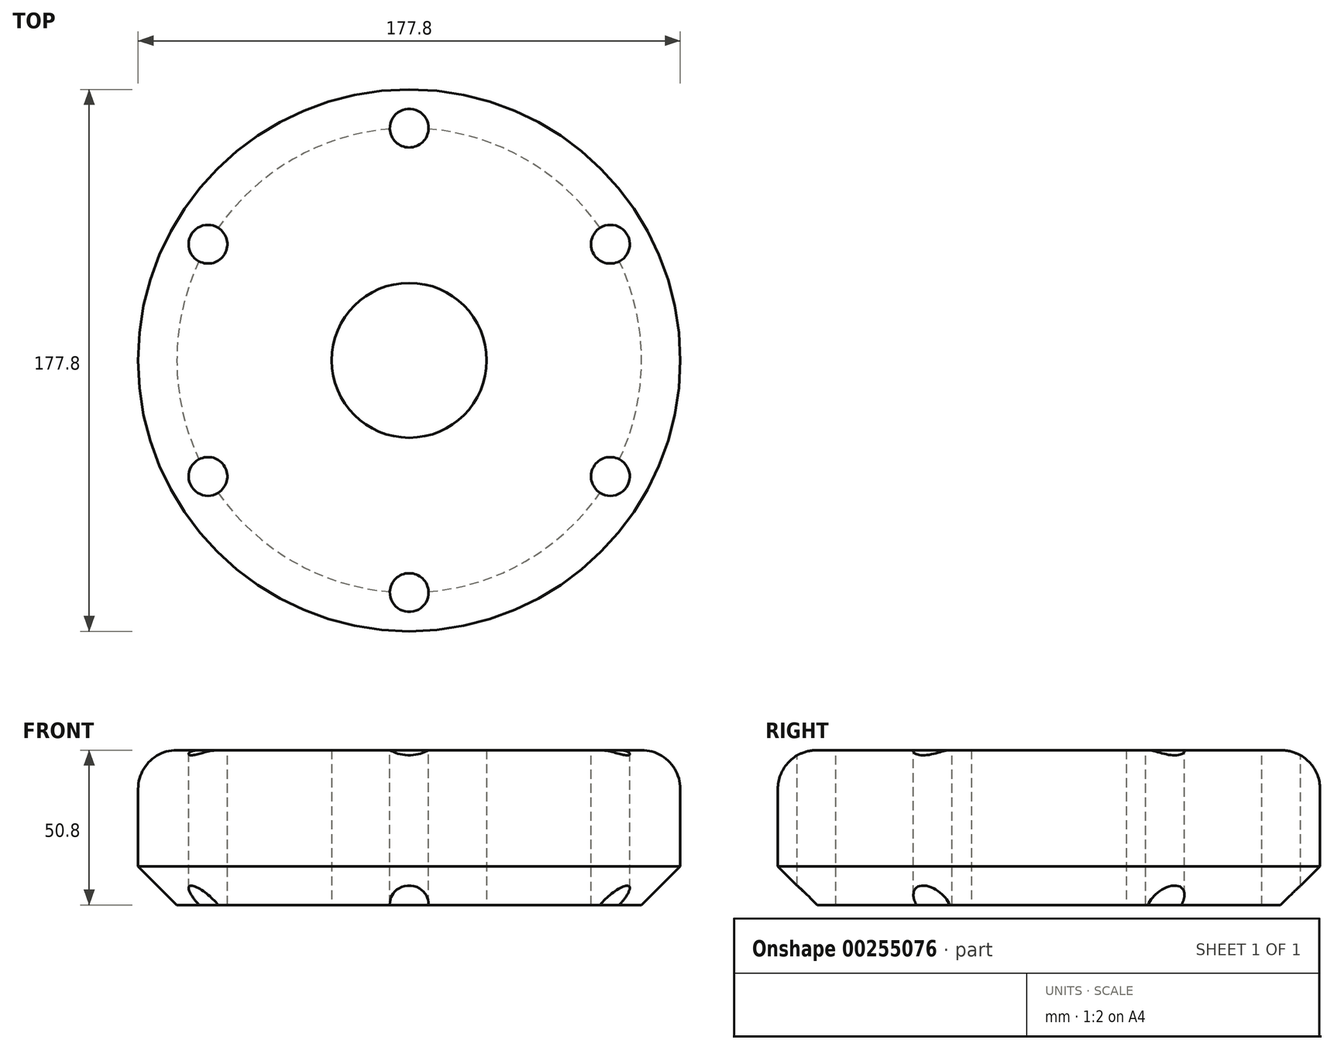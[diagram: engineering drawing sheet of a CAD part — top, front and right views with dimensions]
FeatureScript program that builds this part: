
annotation { "Feature Type Name" : "Feature", "Feature Type Description" : "" }
export const myFeature = defineFeature(function(context is Context, id is Id, definition is map)
    precondition{}
    {
        {
            var Q0;
            Q0=qCreatedBy(makeId("Front.planeOp"),FACE);
            var sketch = newSketch(context, id + "F0", { "sketchPlane" : qUnion([Q0])});
            skLineSegment(sketch, "E0", {"start": v(0, 0) * mm, "end": v(0, 127) * mm});
            skLineSegment(sketch, "E1.bottom", {"start": v(25.4, 0) * mm, "end": v(88.9, 0) * mm});
            skLineSegment(sketch, "E1.top", {"start": v(25.4, 50.8) * mm, "end": v(88.9, 50.8) * mm});
            skLineSegment(sketch, "E1.left", {"start": v(25.4, 0) * mm, "end": v(25.4, 50.8) * mm});
            skLineSegment(sketch, "E1.right", {"start": v(88.9, 0) * mm, "end": v(88.9, 50.8) * mm});
            skSolve(sketch);
        }
        {
            var Q0;
            Q0=makeQuery(id+"F0.imprint","IMPRINT",FACE,{"disambiguationData":[TD([[makeQuery(id+"F0.imprint","IMPRINT",EDGE,{"derivedFrom":sQuery(id+"F0.wireOp",EDGE,"E1.bottom")}),1.0]])]});
            var Q1;
            Q1=sQuery(id+"F0.wireOp",EDGE,"E0");
            revolve(context, id + "F1", {"entities" : qUnion([Q0]), "axis" : qUnion([Q1]), "revolveType" : RevolveType.FULL});
        }
        {
            var Q0;
            Q0=makeQuery(id+"F1.opRevolve","SWEPT_FACE",FACE,{"disambiguationData":[OSD([sQuery(id+"F0.wireOp",EDGE,"E1.top")])]});
            cPlane(context, id + "F2", {"entities" : qUnion([Q0]), "cplaneType" : CPlaneType.OFFSET, "offset" : 25.4 * mm, "width" : 152.4 * mm, "height" : 152.4 * mm});
        }
        {
            var Q0;
            Q0=qCreatedBy(id+"F2.planeOp",FACE);
            var sketch = newSketch(context, id + "F3", { "sketchPlane" : qUnion([Q0])});
            skCircle(sketch, "E2", {"center": v(0, 0) * mm, "radius": 76.2 * mm});
            skLineSegment(sketch, "E3", {"start": v(0, 0) * mm, "end": v(0, 76.2) * mm});
            skCircle(sketch, "E4", {"center": v(0, 76.2) * mm, "radius": 6.35 * mm});
            skCircle(sketch, "E5.1.0", {"center": v(66, 38.1) * mm, "radius": 6.35 * mm});
            skCircle(sketch, "E5.2.0", {"center": v(66, -38.1) * mm, "radius": 6.35 * mm});
            skCircle(sketch, "E5.3.0", {"center": v(0, -76.2) * mm, "radius": 6.35 * mm});
            skCircle(sketch, "E5.4.0", {"center": v(-66, -38.1) * mm, "radius": 6.35 * mm});
            skCircle(sketch, "E5.5.0", {"center": v(-66, 38.1) * mm, "radius": 6.35 * mm});
            skLineSegment(sketch, "E5.anchor1", {"start": v(0, 0) * mm, "end": v(0, 76.2) * mm, "construction": true});
            skLineSegment(sketch, "E5.anchor2", {"start": v(0, 0) * mm, "end": v(-66, 38.1) * mm, "construction": true});
            skSolve(sketch);
        }
        {
            var Q0;
            {var subQ0=sQuery(id+"F3.wireOp",EDGE,"E2");var subQ1=makeQuery(id+"F3.imprint","INTERSECT",VERTEX,{"derivedFrom":[subQ0,sQuery(id+"F3.wireOp",EDGE,"E3")]});Q0=makeQuery(id+"F3.imprint","IMPRINT",FACE,{"disambiguationData":[TD([[makeQuery(id+"F3.imprint","IMPRINT",EDGE,{"disambiguationData":[TD([[subQ1,1.0]])],"derivedFrom":subQ0}),-1.0]])]});}
            var Q1;
            {var subQ0=sQuery(id+"F3.wireOp",EDGE,"E3");var subQ1=sQuery(id+"F3.wireOp",EDGE,"E2");var subQ2=makeQuery(id+"F3.imprint","INTERSECT",VERTEX,{"derivedFrom":[subQ1,subQ0]});Q1=makeQuery(id+"F3.imprint","IMPRINT",FACE,{"disambiguationData":[TD([[makeQuery(id+"F3.imprint","IMPRINT",EDGE,{"disambiguationData":[TD([[subQ2,-1.0]])],"derivedFrom":subQ1}),1.0]])]});}
            var Q2;
            {var subQ0=sQuery(id+"F3.wireOp",EDGE,"E3");var subQ1=sQuery(id+"F3.wireOp",EDGE,"E2");var subQ2=makeQuery(id+"F3.imprint","INTERSECT",VERTEX,{"derivedFrom":[subQ1,subQ0]});Q2=makeQuery(id+"F3.imprint","IMPRINT",FACE,{"disambiguationData":[TD([[makeQuery(id+"F3.imprint","IMPRINT",EDGE,{"disambiguationData":[TD([[subQ2,1.0]])],"derivedFrom":subQ1}),1.0]])]});}
            var Q3;
            {var subQ0=sQuery(id+"F3.wireOp",EDGE,"E5.1.0");var subQ1=sQuery(id+"F3.wireOp",EDGE,"E2");var subQ2=makeQuery(id+"F3.imprint","INTERSECT",VERTEX,{"disambiguationData":[OD(0.0)],"derivedFrom":[subQ1,subQ0]});Q3=makeQuery(id+"F3.imprint","IMPRINT",FACE,{"disambiguationData":[TD([[makeQuery(id+"F3.imprint","IMPRINT",EDGE,{"disambiguationData":[TD([[subQ2,1.0]])],"derivedFrom":subQ1}),-1.0]])]});}
            var Q4;
            {var subQ0=sQuery(id+"F3.wireOp",EDGE,"E5.1.0");var subQ1=sQuery(id+"F3.wireOp",EDGE,"E2");var subQ2=makeQuery(id+"F3.imprint","INTERSECT",VERTEX,{"disambiguationData":[OD(0.0)],"derivedFrom":[subQ1,subQ0]});Q4=makeQuery(id+"F3.imprint","IMPRINT",FACE,{"disambiguationData":[TD([[makeQuery(id+"F3.imprint","IMPRINT",EDGE,{"disambiguationData":[TD([[subQ2,1.0]])],"derivedFrom":subQ1}),1.0]])]});}
            var Q5;
            {var subQ0=sQuery(id+"F3.wireOp",EDGE,"E5.2.0");var subQ1=sQuery(id+"F3.wireOp",EDGE,"E2");var subQ2=makeQuery(id+"F3.imprint","INTERSECT",VERTEX,{"disambiguationData":[OD(0.0)],"derivedFrom":[subQ1,subQ0]});Q5=makeQuery(id+"F3.imprint","IMPRINT",FACE,{"disambiguationData":[TD([[makeQuery(id+"F3.imprint","IMPRINT",EDGE,{"disambiguationData":[TD([[subQ2,-1.0]])],"derivedFrom":subQ1}),1.0]])]});}
            var Q6;
            {var subQ0=sQuery(id+"F3.wireOp",EDGE,"E5.2.0");var subQ1=sQuery(id+"F3.wireOp",EDGE,"E2");var subQ2=makeQuery(id+"F3.imprint","INTERSECT",VERTEX,{"disambiguationData":[OD(0.0)],"derivedFrom":[subQ1,subQ0]});Q6=makeQuery(id+"F3.imprint","IMPRINT",FACE,{"disambiguationData":[TD([[makeQuery(id+"F3.imprint","IMPRINT",EDGE,{"disambiguationData":[TD([[subQ2,-1.0]])],"derivedFrom":subQ1}),-1.0]])]});}
            var Q7;
            {var subQ0=sQuery(id+"F3.wireOp",EDGE,"E5.3.0");var subQ1=sQuery(id+"F3.wireOp",EDGE,"E2");var subQ2=makeQuery(id+"F3.imprint","INTERSECT",VERTEX,{"disambiguationData":[OD(0.0)],"derivedFrom":[subQ1,subQ0]});Q7=makeQuery(id+"F3.imprint","IMPRINT",FACE,{"disambiguationData":[TD([[makeQuery(id+"F3.imprint","IMPRINT",EDGE,{"disambiguationData":[TD([[subQ2,-1.0]])],"derivedFrom":subQ1}),1.0]])]});}
            var Q8;
            {var subQ0=sQuery(id+"F3.wireOp",EDGE,"E5.3.0");var subQ1=sQuery(id+"F3.wireOp",EDGE,"E2");var subQ2=makeQuery(id+"F3.imprint","INTERSECT",VERTEX,{"disambiguationData":[OD(0.0)],"derivedFrom":[subQ1,subQ0]});Q8=makeQuery(id+"F3.imprint","IMPRINT",FACE,{"disambiguationData":[TD([[makeQuery(id+"F3.imprint","IMPRINT",EDGE,{"disambiguationData":[TD([[subQ2,-1.0]])],"derivedFrom":subQ1}),-1.0]])]});}
            var Q9;
            {var subQ0=sQuery(id+"F3.wireOp",EDGE,"E5.4.0");var subQ1=sQuery(id+"F3.wireOp",EDGE,"E2");var subQ2=makeQuery(id+"F3.imprint","INTERSECT",VERTEX,{"disambiguationData":[OD(0.0)],"derivedFrom":[subQ1,subQ0]});Q9=makeQuery(id+"F3.imprint","IMPRINT",FACE,{"disambiguationData":[TD([[makeQuery(id+"F3.imprint","IMPRINT",EDGE,{"disambiguationData":[TD([[subQ2,-1.0]])],"derivedFrom":subQ1}),-1.0]])]});}
            var Q10;
            {var subQ0=sQuery(id+"F3.wireOp",EDGE,"E5.4.0");var subQ1=sQuery(id+"F3.wireOp",EDGE,"E2");var subQ2=makeQuery(id+"F3.imprint","INTERSECT",VERTEX,{"disambiguationData":[OD(0.0)],"derivedFrom":[subQ1,subQ0]});Q10=makeQuery(id+"F3.imprint","IMPRINT",FACE,{"disambiguationData":[TD([[makeQuery(id+"F3.imprint","IMPRINT",EDGE,{"disambiguationData":[TD([[subQ2,-1.0]])],"derivedFrom":subQ1}),1.0]])]});}
            var Q11;
            {var subQ0=sQuery(id+"F3.wireOp",EDGE,"E5.5.0");var subQ1=sQuery(id+"F3.wireOp",EDGE,"E2");var subQ2=makeQuery(id+"F3.imprint","INTERSECT",VERTEX,{"disambiguationData":[OD(0.0)],"derivedFrom":[subQ1,subQ0]});Q11=makeQuery(id+"F3.imprint","IMPRINT",FACE,{"disambiguationData":[TD([[makeQuery(id+"F3.imprint","IMPRINT",EDGE,{"disambiguationData":[TD([[subQ2,-1.0]])],"derivedFrom":subQ1}),-1.0]])]});}
            var Q12;
            {var subQ0=sQuery(id+"F3.wireOp",EDGE,"E5.5.0");var subQ1=sQuery(id+"F3.wireOp",EDGE,"E2");var subQ2=makeQuery(id+"F3.imprint","INTERSECT",VERTEX,{"disambiguationData":[OD(0.0)],"derivedFrom":[subQ1,subQ0]});Q12=makeQuery(id+"F3.imprint","IMPRINT",FACE,{"disambiguationData":[TD([[makeQuery(id+"F3.imprint","IMPRINT",EDGE,{"disambiguationData":[TD([[subQ2,-1.0]])],"derivedFrom":subQ1}),1.0]])]});}
            extrude(context, id + "F4", {"entities" : qUnion([Q0, Q1, Q2, Q3, Q4, Q5, Q6, Q7, Q8, Q9, Q10, Q11, Q12]), "operationType" : NewBodyOperationType.REMOVE, "endBound" : BoundingType.THROUGH_ALL, "oppositeDirection" : true, "depth" : 25.4 * mm});
        }
        {
            var Q0;
            Q0=makeQuery(id+"F1.opRevolve","SWEPT_EDGE",EDGE,{"disambiguationData":[OSD([sQuery(id+"F0.wireOp",EDGE,"E1.top"),sQuery(id+"F0.wireOp",EDGE,"E1.right")])]});
            fillet(context, id + "F5", {"entities" : qUnion([Q0]), "radius" : 12.7 * mm, "tangentPropagation" : true, "allowEdgeOverflow" : false});
        }
        {
            var Q0;
            Q0=makeQuery(id+"F1.opRevolve","SWEPT_FACE",FACE,{"disambiguationData":[OSD([sQuery(id+"F0.wireOp",EDGE,"E1.right")])]});
            chamfer(context, id + "F6", {"entities" : qUnion([Q0]), "width" : 12.7 * mm, "tangentPropagation" : true});
        }
    });
